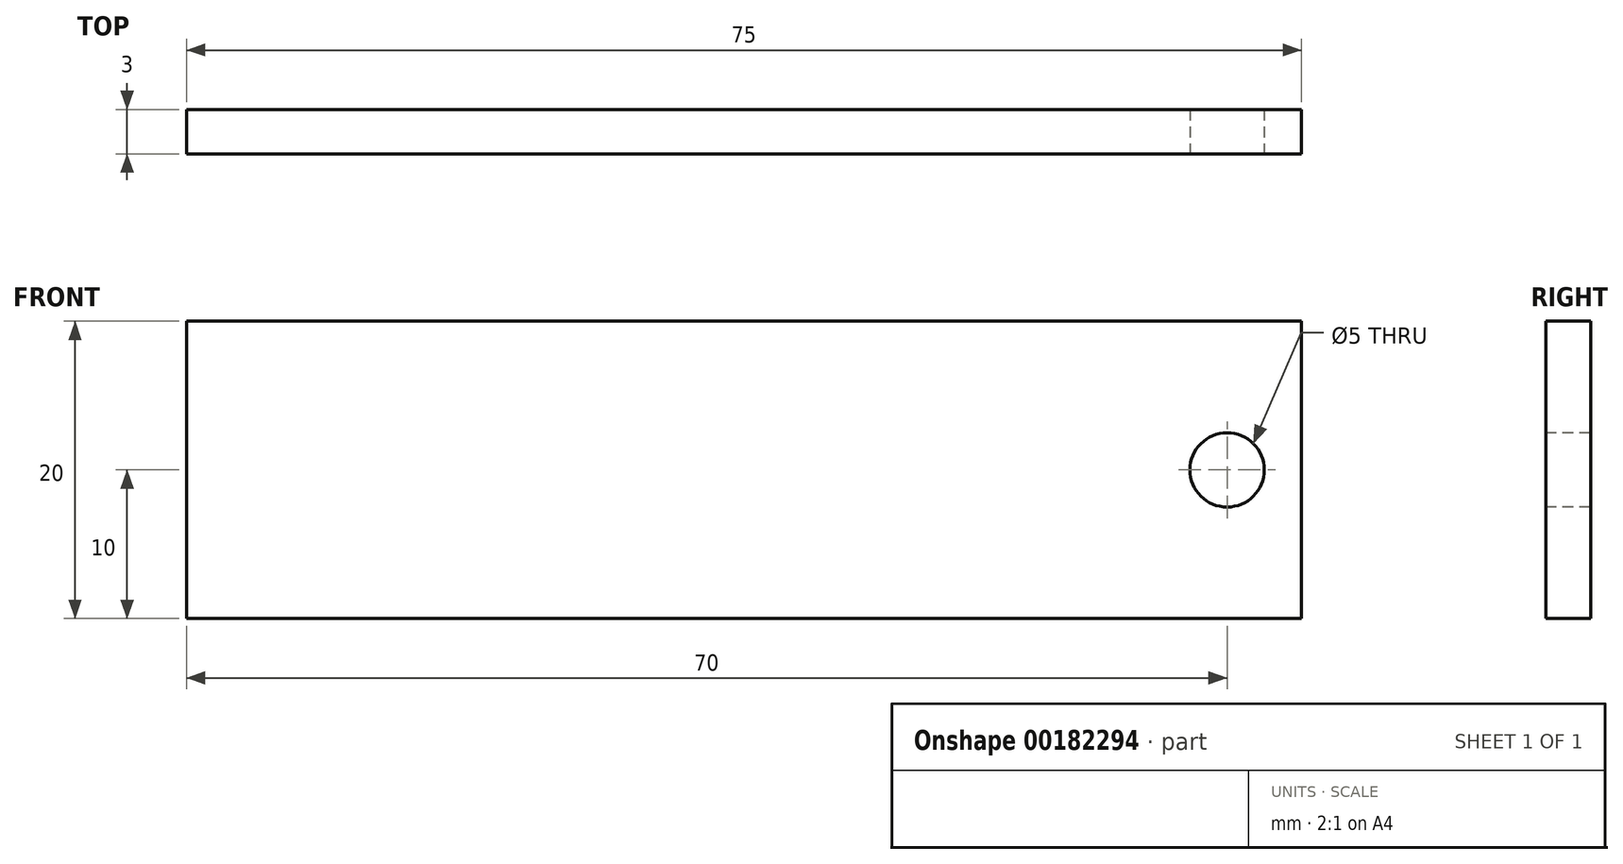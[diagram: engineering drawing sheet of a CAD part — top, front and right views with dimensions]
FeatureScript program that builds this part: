
annotation { "Feature Type Name" : "Feature", "Feature Type Description" : "" }
export const myFeature = defineFeature(function(context is Context, id is Id, definition is map)
    precondition{}
    {
        {
            var Q0;
            Q0=qCreatedBy(makeId("Front.planeOp"),FACE);
            var sketch = newSketch(context, id + "F0", { "sketchPlane" : qUnion([Q0])});
            skLineSegment(sketch, "E0.bottom", {"start": v(0, 0) * mm, "end": v(75, 0) * mm});
            skLineSegment(sketch, "E0.top", {"start": v(0, -20) * mm, "end": v(75, -20) * mm});
            skLineSegment(sketch, "E0.left", {"start": v(0, 0) * mm, "end": v(0, -20) * mm});
            skLineSegment(sketch, "E0.right", {"start": v(75, 0) * mm, "end": v(75, -20) * mm});
            skCircle(sketch, "E1", {"center": v(70, -10) * mm, "radius": 2.5 * mm});
            skSolve(sketch);
        }
        {
            var Q0;
            Q0 = qSketchRegion(id + "F0", true);
            extrude(context, id + "F1", {"entities" : qUnion([Q0]), "oppositeDirection" : true, "depth" : 3 * mm});
        }
    });
